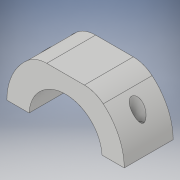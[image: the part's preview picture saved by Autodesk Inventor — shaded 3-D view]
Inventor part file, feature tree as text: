
AUTODESK INVENTOR PART (.ipt)
format: ipt  version: 2019 (Build 230136000, 136)  size: 153,088 bytes
history: native  units: mm
features: sketch x4, extrude x3, hole x1, fillet x1
ambient origin geometry x8: Origin, YZ Plane, XZ Plane, XY Plane, X Axis, Y Axis, Z Axis, Center Point
bodies: Solid1 (feature_tree)
feature tree (9):
  extrude  "Extrusion1"  Depth=60.0mm
  extrude  "Extrusion2"  Depth=25.0mm TaperAngle=0.0deg
  sketch  "Sketch3"  dims[d5=1.0mm d6=10.0mm d7=0.0mm]
  extrude  "Extrusion3"  Depth=10.0mm TaperAngle=0.0deg
  hole  "Hole2"  [1 undecoded]
  fillet  "Fillet2"  [1 undecoded]
  sketch  "Sketch1"  dims[d0=37.35mm d1=60.0mm]
  sketch  "Sketch2"  dims[d2=55.0mm d3=25.0mm d4=0.0mm]
  sketch  "Sketch4"  dims[d16=10.0mm d17=0.0mm d18=3.175mm d19=6.0mm d20=6.1mm d21=17.0mm d22=90.0deg d23=8.0mm d24=90.0deg d25=15.0mm]
note: 2 required parameter values undecoded (feature->parameter linkage not recoverable at this tier; creation-order binding heuristic only, values carry confidence <= 0.55)
